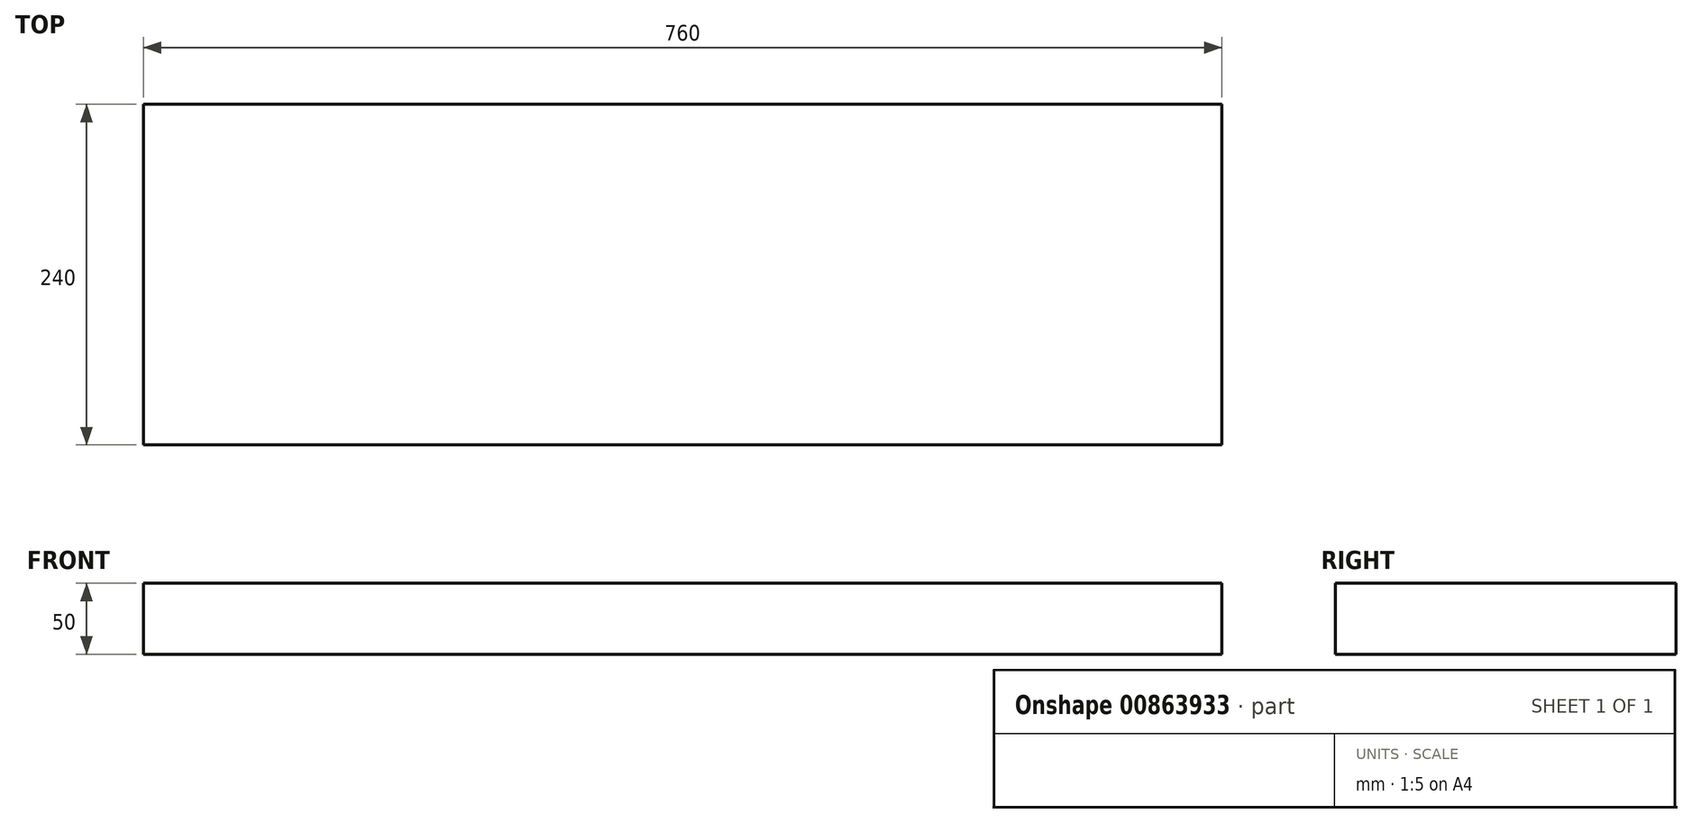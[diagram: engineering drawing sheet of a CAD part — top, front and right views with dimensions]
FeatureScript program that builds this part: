
annotation { "Feature Type Name" : "Feature", "Feature Type Description" : "" }
export const myFeature = defineFeature(function(context is Context, id is Id, definition is map)
    precondition{}
    {
        {
            var Q0;
            Q0=qCreatedBy(makeId("Top.planeOp"),FACE);
            var sketch = newSketch(context, id + "F0", { "sketchPlane" : qUnion([Q0])});
            skLineSegment(sketch, "E0", {"start": v(-380, 120) * mm, "end": v(-380, -120) * mm});
            skLineSegment(sketch, "E1", {"start": v(380, 120) * mm, "end": v(380, -120) * mm});
            skLineSegment(sketch, "E2", {"start": v(380, -120) * mm, "end": v(-380, -120) * mm});
            skLineSegment(sketch, "E3", {"start": v(-380, 120) * mm, "end": v(380, 120) * mm});
            skSolve(sketch);
        }
        {
            var Q0;
            Q0=makeQuery(id+"F0.imprint","IMPRINT",FACE,{"disambiguationData":[TD([[makeQuery(id+"F0.imprint","IMPRINT",EDGE,{"derivedFrom":sQuery(id+"F0.wireOp",EDGE,"E0")}),1.0]])]});
            extrude(context, id + "F1", {"entities" : qUnion([Q0]), "depth" : 50 * mm, "offsetDistance" : 25 * mm});
        }
    });
